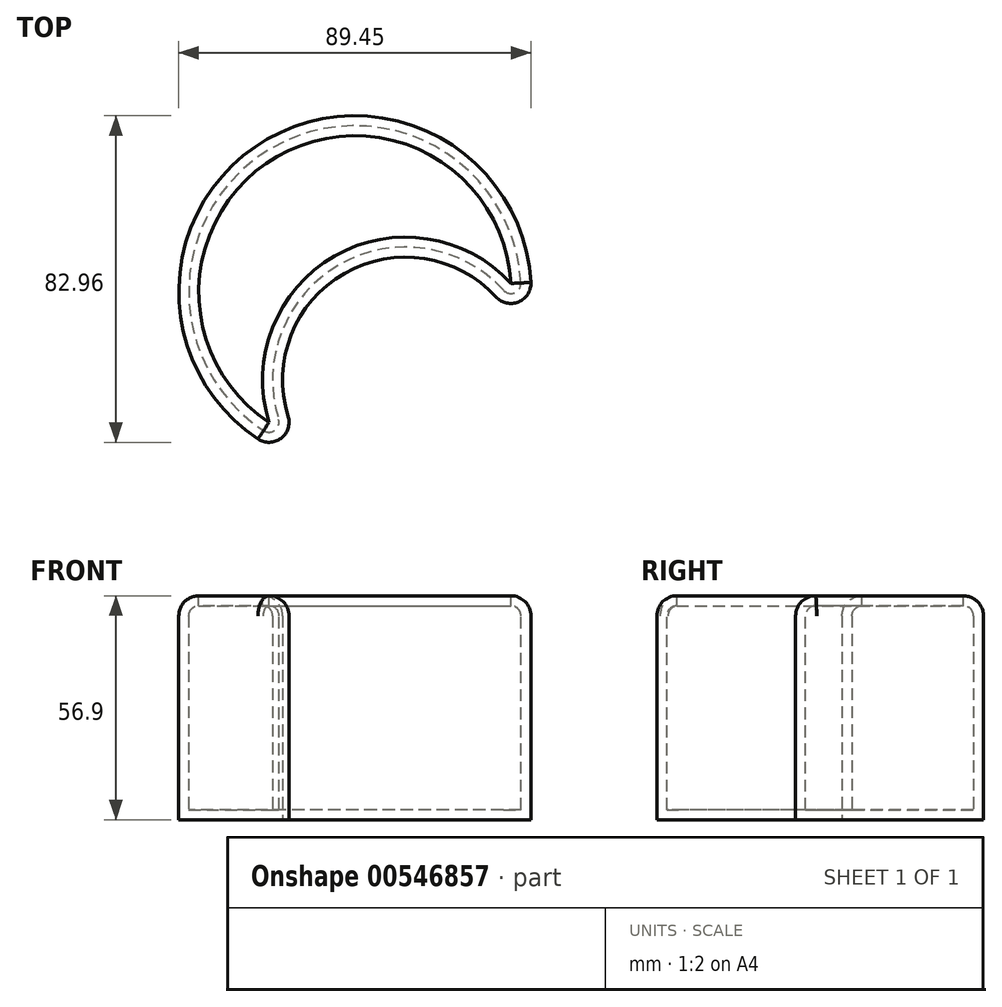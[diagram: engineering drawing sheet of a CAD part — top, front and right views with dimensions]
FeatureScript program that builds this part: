
annotation { "Feature Type Name" : "Feature", "Feature Type Description" : "" }
export const myFeature = defineFeature(function(context is Context, id is Id, definition is map)
    precondition{}
    {
        {
            var Q0;
            Q0=qCreatedBy(makeId("Top.planeOp"),FACE);
            var sketch = newSketch(context, id + "F0", { "sketchPlane" : qUnion([Q0])});
            skCircle(sketch, "E0", {"center": v(-12.85, 22.39) * mm, "radius": 44.75 * mm});
            skCircle(sketch, "E1", {"center": v(0, 0) * mm, "radius": 31.22 * mm});
            skSolve(sketch);
        }
        {
            var Q0;
            {var subQ0=sQuery(id+"F0.wireOp",EDGE,"E1");var subQ1=sQuery(id+"F0.wireOp",EDGE,"E0");var subQ2=makeQuery(id+"F0.imprint","INTERSECT",VERTEX,{"disambiguationData":[OD(0.0)],"derivedFrom":[subQ1,subQ0]});Q0=makeQuery(id+"F0.imprint","IMPRINT",FACE,{"disambiguationData":[TD([[makeQuery(id+"F0.imprint","IMPRINT",EDGE,{"disambiguationData":[TD([[subQ2,1.0]])],"derivedFrom":subQ1}),1.0]])]});}
            extrude(context, id + "F1", {"entities" : qUnion([Q0]), "depth" : 56.9 * mm, "offsetDistance" : 25.4 * mm});
        }
        {
            var Q0;
            Q0=makeQuery(id+"F1.opExtrude","CAP_EDGE",EDGE,{"disambiguationData":[OSD([sQuery(id+"F0.wireOp",EDGE,"E0")])],"isStart":false});
            fillet(context, id + "F2", {"entities" : qUnion([Q0]), "tangentPropagation" : true, "radius" : 5.08 * mm, "defaultsChanged" : false, "vertexSettings" : [], "allowEdgeOverflow" : false});
        }
        {
            var Q0;
            Q0=makeQuery(id+"F1.opExtrude","CAP_EDGE",EDGE,{"disambiguationData":[OSD([sQuery(id+"F0.wireOp",EDGE,"E1")])],"isStart":false});
            fillet(context, id + "F3", {"entities" : qUnion([Q0]), "tangentPropagation" : true, "radius" : 5.08 * mm, "defaultsChanged" : false, "vertexSettings" : [], "allowEdgeOverflow" : false});
        }
        {
            var Q0;
            Q0=makeQuery(id+"F1.opExtrude","CAP_FACE",FACE,{"disambiguationData":[OSD([sQuery(id+"F0.wireOp",EDGE,"E0"),sQuery(id+"F0.wireOp",EDGE,"E1")])],"isStart":false});
            shell(context, id + "F4", {"entities" : qUnion([Q0]), "thickness" : 2.54 * mm});
        }
    });
